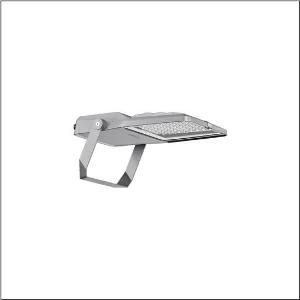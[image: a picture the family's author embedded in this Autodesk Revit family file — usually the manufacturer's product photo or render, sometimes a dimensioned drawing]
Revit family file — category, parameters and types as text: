
# Revit family: floodlight_fl_21_iq_mini___rs12_5xa7772b1b1a_07b1
name_source: partatom
category: Lighting Fixtures
units: mm (PartAtom-declared; Revit-internal decimal feet)

## family parameters
Cut with Voids When Loaded = No
Host = Face
Light Source = No
Part Type = Normal
Room Calculation Point = No
Round Connector Dimension = Use Diameter
Shared = No

## types (1)
- --- (1 x LED, 5230 lm, 45.5 W, 2200K)
    Apparent Load = 46 VA
    CIE Flux Codes = 79 92 99 100 100
    Color Rendering = 70
    Color Temperature = 2200K
    Default Elevation = 1800 mm
    Description = Floodlight FL 21 iQ mini, floodlight, primary light control with lens, of PMMA, primary optical cover: protective disc, of toughened safety glass, transparent, light distribution: RS12, light emission: direct distribution, installation type: surface-mounted, lamps: LED, High Power LED, rated values: 5.230lm | 45,5W | 114,9lm/W (begin service life); end service life: 5.230lm | 48W; at 50% lumin. flux: 2.615lm | 21,4W | 122,2lm/W, colour temperature: 2200K, colour rendering: CRI > 70, light colour: 722, light setting 1 begin service life: 100% | 5.230lm | 45,5W | 114,9lm/W | 2.200K, light setting 1 end service life: 48W, further light settings possible, control: Street-Remote, Auto-Match, Temp-Guard, Night-Set, Smart-Wire, Desk-Remote (wireless, voltage-free reading and setting of iQ features in the workshop via application-optimized NFC function/RFID function), optimised constant luminous flux control (CLO 2.0), pre-setting: linear dimming characteristic, with terminal, 6-pole, mains connection: 220..240V, AC, 50/60Hz, luminaire housing, of diecast aluminium, powder-coated, SITECO metallic grey (DB 702S), corrosivity category C5 mid according to DIN EN ISO 12944suitable for swimming poolschlorine-resistant, sealing non-destructively replaceable, mounting bracket, of steel, galvanised, powder-coated, SITECO metallic grey (DB 702S), protection rating (complete): IP66, insulation class (complete): insulation class II (safety insulation), certification: CE, ENEC, VDE, protection symbol: D, impact resistance: IK08, permissible operating ambient temperature: -40..+40°C, permissible operating ambient temperature for outdoor applications: -40..+50°C, standard: DIN EN 12944, LABS conformity tested according to VDMA 24364:2018-05, packaging unit: 1 piece

Light Distribution: RS12
    Height = 70 mm
    Lamp = 1 x LED
    Lamp Light Flux = 5230 lm
    Lamp Power = 45.5 W
    Lamp count = 1
    Length = 485 mm
    Luminous efficacy = 115 lm/W
    Manufacturer = Siteco
    ModVariant = No
    Model = 5XA7772B1B1A
    Mounting Place = Pole
    Mounting Type = Pole annexe
    Number of Poles = 1
    OnlyDefault = Yes
    Power Factor = 1
    Product Name = Floodlight FL 21 iQ mini | RS12
    Product group = floodlight | pylon annexe
    ProductGroupID = 6201
    Protection Class = Protection class II
    Protection Degree = IP 66
    RLX_Detail_Level = 1
    RLX_Emergency_Light_Flux = 0 lm
    RLX_Emergency_Type = 0
    RLX_Emergency_Type_DB = No
    RlxData = <blob elided: 91249 chars, md5=2bb0735c>
    Socket = socket
    Standby Power = 0 W
    System Light Flux = 5230 lm
    System Power = 46 W
    Type Comments = factory setting: luminous flux: 100 % | dim-lin: 254 | 463 mA
    Type Image = l_1006845.jpg
    URL = http://relux.com
    VarID = @adj_168957
    Voltage = 0 V
    Weight = 0.00 kg
    Width = 337 mm

## geometry (parser evidence)
native form markers: Blend x4, Sweep x14
no freeform markers — native parametric forms only
